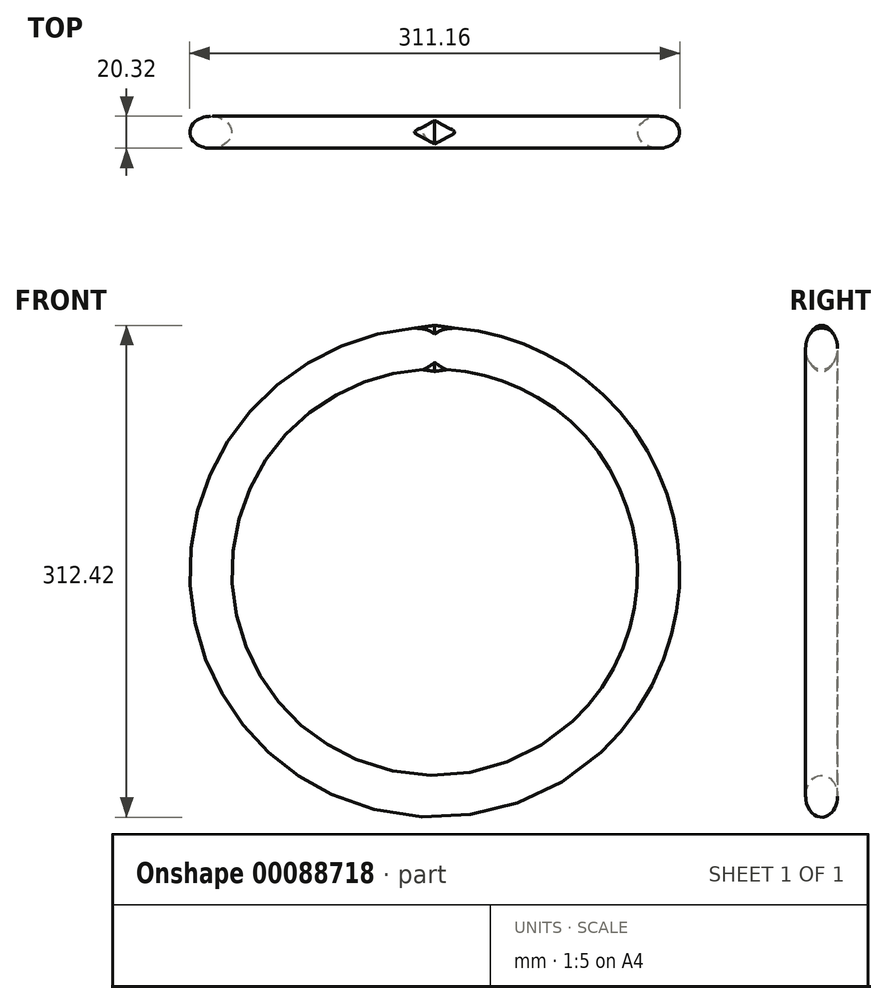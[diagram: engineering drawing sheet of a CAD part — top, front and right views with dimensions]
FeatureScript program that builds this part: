
annotation { "Feature Type Name" : "Feature", "Feature Type Description" : "" }
export const myFeature = defineFeature(function(context is Context, id is Id, definition is map)
    precondition{}
    {
        {
            var Q0;
            Q0=qCreatedBy(makeId("Top.planeOp"),FACE);
            var sketch = newSketch(context, id + "F0", { "sketchPlane" : qUnion([Q0])});
            skLineSegment(sketch, "E0", {"start": v(0, 0) * mm, "end": v(0, -41.48) * mm});
            skEllipse(sketch, "E1", {"center": v(-142.24, 0) * mm, "majorRadius": 10.16 * mm, "minorRadius": 13.34 * mm, "majorAxis": v(0, -1)});
            skSolve(sketch);
        }
        {
            var Q0;
            Q0=makeQuery(id+"F0.imprint","IMPRINT",FACE,{"disambiguationData":[TD([[makeQuery(id+"F0.imprint","IMPRINT",EDGE,{"derivedFrom":sQuery(id+"F0.wireOp",EDGE,"qveeLJNj-zh7h-TVlV-G7u6-FEW5EJjQTrcv")}),1.0]])]});
            var Q1;
            Q1=makeQuery(id+"F0.imprint","IMPRINT",FACE,{"disambiguationData":[TD([[makeQuery(id+"F0.imprint","IMPRINT",EDGE,{"derivedFrom":sQuery(id+"F0.wireOp",EDGE,"E1")}),1.0]])]});
            var Q2;
            Q2=sQuery(id+"F0.wireOp",EDGE,"E0");
            revolve(context, id + "F1", {"entities" : qUnion([Q0, Q1]), "axis" : qUnion([Q2]), "revolveType" : RevolveType.FULL});
        }
        {
            var Q0;
            Q0=qCreatedBy(makeId("Right.planeOp"),FACE);
            var sketch = newSketch(context, id + "F2", { "sketchPlane" : qUnion([Q0])});
            skEllipse(sketch, "E2", {"center": v(0, 142.24) * mm, "majorRadius": 14.6 * mm, "minorRadius": 9.53 * mm, "majorAxis": v(0, -1)});
            skSolve(sketch);
        }
        {
            var Q0;
            Q0=makeQuery(id+"F2.imprint","IMPRINT",FACE,{"disambiguationData":[TD([[makeQuery(id+"F2.imprint","IMPRINT",EDGE,{"derivedFrom":sQuery(id+"F2.wireOp",EDGE,"E2")}),1.0]])]});
            extrude(context, id + "F3", {"entities" : qUnion([Q0]), "operationType" : NewBodyOperationType.ADD, "depth" : 12.7 * mm, "hasDraft" : true, "draftAngle" : 8 * degree, "draftPullDirection" : true, "hasSecondDirection" : true, "secondDirectionOppositeDirection" : true, "secondDirectionDepth" : 12.7 * mm, "hasSecondDirectionDraft" : true, "secondDirectionDraftAngle" : 8 * degree, "secondDirectionDraftPullDirection" : true});
        }
    });
